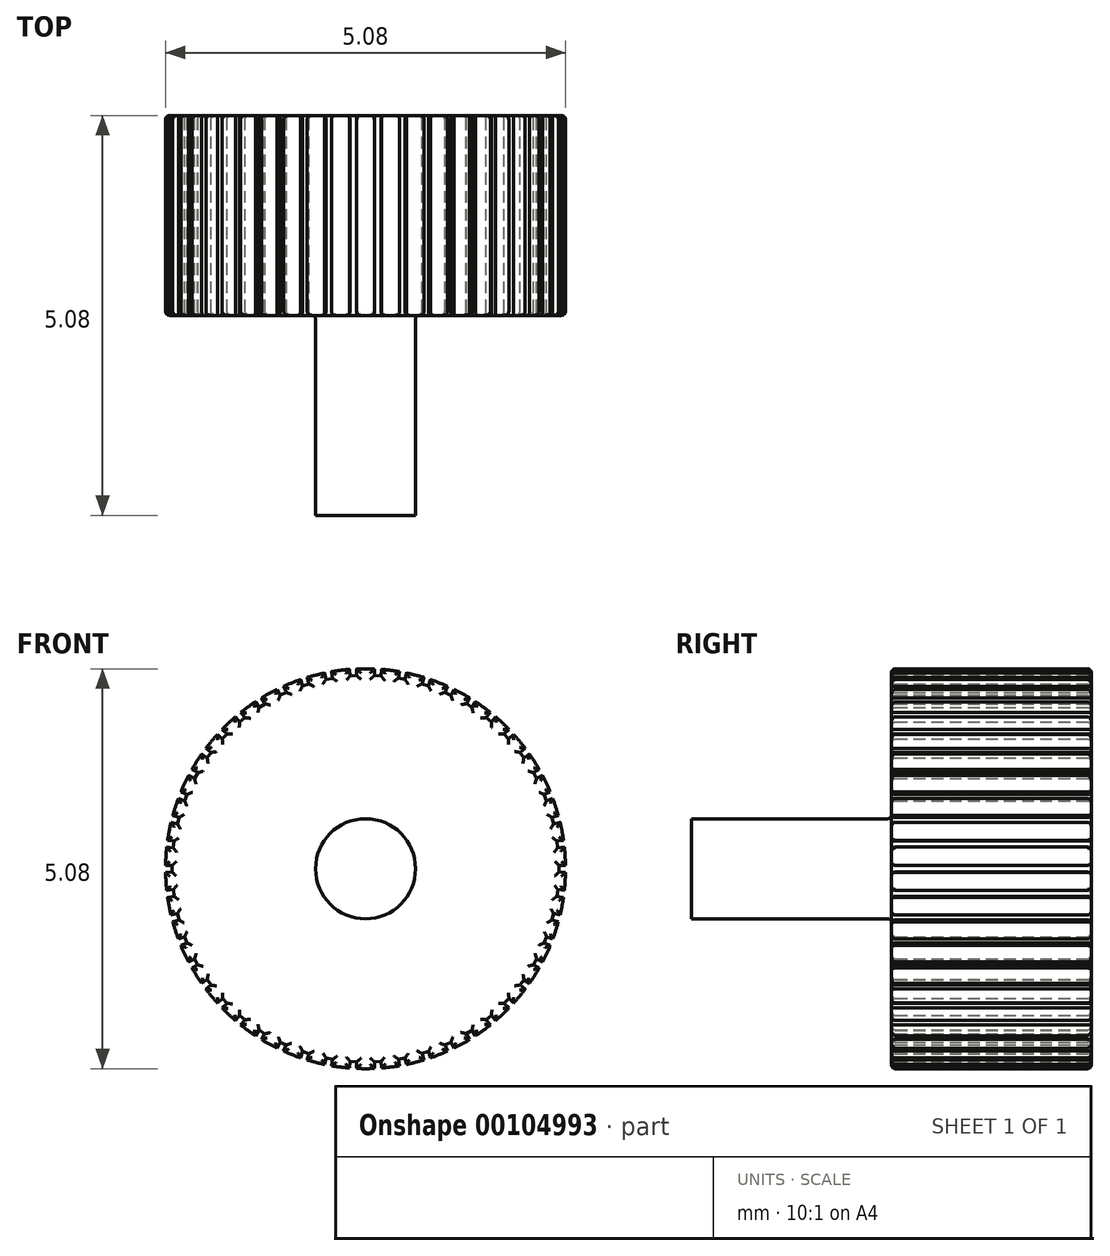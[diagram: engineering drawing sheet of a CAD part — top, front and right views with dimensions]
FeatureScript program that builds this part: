
annotation { "Feature Type Name" : "Feature", "Feature Type Description" : "" }
export const myFeature = defineFeature(function(context is Context, id is Id, definition is map)
    precondition{}
    {
        {
            var Q0;
            Q0=qCreatedBy(makeId("Front.planeOp"),FACE);
            var sketch = newSketch(context, id + "F0", { "sketchPlane" : qUnion([Q0])});
            skCircle(sketch, "E0", {"center": v(0, 0) * mm, "radius": 2.54 * mm});
            skSolve(sketch);
        }
        {
            var Q0;
            Q0=makeQuery(id+"F0.imprint","IMPRINT",FACE,{"disambiguationData":[TD([[makeQuery(id+"F0.imprint","IMPRINT",EDGE,{"derivedFrom":sQuery(id+"F0.wireOp",EDGE,"E0")}),1.0]])]});
            extrude(context, id + "F1", {"entities" : qUnion([Q0]), "depth" : 2.54 * mm});
        }
        {
            var Q0;
            Q0=makeQuery(id+"F1.opExtrude","CAP_FACE",FACE,{"disambiguationData":[OSD([sQuery(id+"F0.wireOp",EDGE,"E0")])],"isStart":false});
            var sketch = newSketch(context, id + "F2", { "sketchPlane" : qUnion([Q0])});
            skCircle(sketch, "E1", {"center": v(0, 0) * mm, "radius": 0.64 * mm});
            skSolve(sketch);
        }
        {
            var Q0;
            Q0=makeQuery(id+"F2.imprint","IMPRINT",FACE,{"disambiguationData":[TD([[makeQuery(id+"F2.imprint","IMPRINT",EDGE,{"derivedFrom":sQuery(id+"F2.wireOp",EDGE,"E1")}),1.0]])]});
            extrude(context, id + "F3", {"entities" : qUnion([Q0]), "operationType" : NewBodyOperationType.ADD, "depth" : 2.54 * mm});
        }
        {
            var Q0;
            Q0=makeQuery(id+"F1.opExtrude","CAP_FACE",FACE,{"disambiguationData":[OSD([sQuery(id+"F0.wireOp",EDGE,"E0")])],"isStart":true});
            var sketch = newSketch(context, id + "F4", { "sketchPlane" : qUnion([Q0])});
            skLineSegment(sketch, "E2", {"start": v(0, 0) * mm, "end": v(-2.54, 0.04) * mm});
            skLineSegment(sketch, "E3.MirrorCS", {"start": v(0, 0) * mm, "end": v(-2.54, -0.04) * mm});
            skLineSegment(sketch, "E4", {"start": v(-2.45, -0.04) * mm, "end": v(-2.46, 0.04) * mm});
            skSolve(sketch);
        }
        {
            var Q0;
            {var subQ3=sQuery(id+"F4.wireOp",EDGE,"E4");Q0=makeQuery(id+"F4.imprint","IMPRINT",FACE,{"disambiguationData":[TD([[makeQuery(id+"F4.imprint","IMPRINT",EDGE,{"derivedFrom":subQ3}),1.0]])]});}
            extrude(context, id + "F5", {"entities" : qUnion([Q0]), "operationType" : NewBodyOperationType.REMOVE, "oppositeDirection" : true, "depth" : 25.4 * mm});
        }
        {
            var Q0;
            Q0=makeQuery(id+"F5.boolean.opBoolean","COPY",FACE,{"derivedFrom":makeQuery(id+"F5.opExtrude","SWEPT_FACE",FACE,{"disambiguationData":[OSD([sQuery(id+"F4.wireOp",EDGE,"E4")])]})});
            var Q1;
            Q1=makeQuery(id+"F5.boolean.opBoolean","COPY",FACE,{"derivedFrom":makeQuery(id+"F5.opExtrude","SWEPT_FACE",FACE,{"disambiguationData":[OSD([sQuery(id+"F4.wireOp",EDGE,"E2")])]})});
            var Q2;
            Q2=makeQuery(id+"F5.boolean.opBoolean","COPY",FACE,{"derivedFrom":makeQuery(id+"F5.opExtrude","SWEPT_FACE",FACE,{"disambiguationData":[OSD([sQuery(id+"F4.wireOp",EDGE,"E3.MirrorCS")])]})});
            var Q3;
            Q3=makeQuery(id+"F1.opExtrude","SWEPT_FACE",FACE,{"disambiguationData":[OSD([sQuery(id+"F0.wireOp",EDGE,"E0")])]});
            circularPattern(context, id + "F6", {"patternType" : PatternType.FACE, "operationType" : NewBodyOperationType.REMOVE, "faces" : qUnion([Q0, Q1, Q2]), "axis" : qUnion([Q3]), "angle" : 360 * degree, "instanceCount" : 50, "equalSpace" : true});
        }
        {
            var Q0;
            Q0=makeQuery(id+"F1.opExtrude","CAP_FACE",FACE,{"disambiguationData":[OSD([sQuery(id+"F0.wireOp",EDGE,"E0")])],"isStart":true});
            fillet(context, id + "F7", {"entities" : qUnion([Q0]), "radius" : 0.05 * mm, "tangentPropagation" : true, "allowEdgeOverflow" : false});
        }
        {
            var Q0;
            Q0=makeQuery(id+"F1.opExtrude","CAP_FACE",FACE,{"disambiguationData":[OSD([sQuery(id+"F0.wireOp",EDGE,"E0")])],"isStart":false});
            fillet(context, id + "F8", {"entities" : qUnion([Q0]), "radius" : 0.05 * mm, "tangentPropagation" : true, "allowEdgeOverflow" : false});
        }
    });
